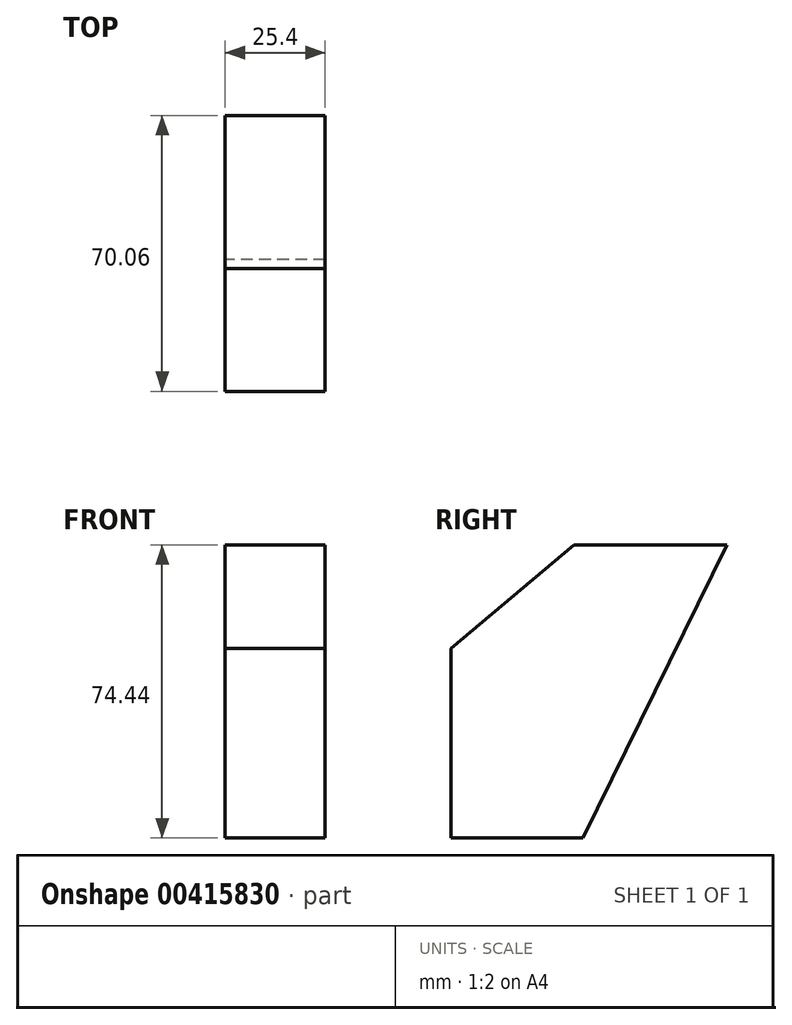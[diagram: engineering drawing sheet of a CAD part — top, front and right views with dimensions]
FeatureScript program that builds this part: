
annotation { "Feature Type Name" : "Feature", "Feature Type Description" : "" }
export const myFeature = defineFeature(function(context is Context, id is Id, definition is map)
    precondition{}
    {
        {
            var Q0;
            Q0=qCreatedBy(makeId("Right.planeOp"),FACE);
            var sketch = newSketch(context, id + "F0", { "sketchPlane" : qUnion([Q0])});
            skLineSegment(sketch, "E0.bottom", {"start": v(0, 0) * mm, "end": v(33.5, 0) * mm});
            skLineSegment(sketch, "E0.top", {"start": v(0, 48.1) * mm, "end": v(33.5, 48.1) * mm});
            skLineSegment(sketch, "E0.left", {"start": v(0, 0) * mm, "end": v(0, 48.1) * mm});
            skLineSegment(sketch, "E0.right", {"start": v(33.5, 0) * mm, "end": v(33.5, 48.1) * mm});
            skLineSegment(sketch, "E1", {"start": v(0, 48.1) * mm, "end": v(31.22, 74.44) * mm});
            skLineSegment(sketch, "E2", {"start": v(31.22, 74.44) * mm, "end": v(33.5, 48.1) * mm});
            skLineSegment(sketch, "E3", {"start": v(33.5, 48.1) * mm, "end": v(70.06, 74.44) * mm});
            skLineSegment(sketch, "E4", {"start": v(70.06, 74.44) * mm, "end": v(33.5, 0) * mm});
            skLineSegment(sketch, "E5", {"start": v(31.22, 74.44) * mm, "end": v(70.06, 74.44) * mm});
            skSolve(sketch);
        }
        {
            var Q0;
            Q0=makeQuery(id+"F0.imprint","IMPRINT",FACE,{"disambiguationData":[TD([[makeQuery(id+"F0.imprint","IMPRINT",EDGE,{"derivedFrom":sQuery(id+"F0.wireOp",EDGE,"E0.top")}),1.0]])]});
            var Q1;
            Q1=makeQuery(id+"F0.imprint","IMPRINT",FACE,{"disambiguationData":[TD([[makeQuery(id+"F0.imprint","IMPRINT",EDGE,{"derivedFrom":sQuery(id+"F0.wireOp",EDGE,"E2")}),1.0]])]});
            var Q2;
            Q2=makeQuery(id+"F0.imprint","IMPRINT",FACE,{"disambiguationData":[TD([[makeQuery(id+"F0.imprint","IMPRINT",EDGE,{"derivedFrom":sQuery(id+"F0.wireOp",EDGE,"E0.right")}),-1.0]])]});
            var Q3;
            Q3=makeQuery(id+"F0.imprint","IMPRINT",FACE,{"disambiguationData":[TD([[makeQuery(id+"F0.imprint","IMPRINT",EDGE,{"derivedFrom":sQuery(id+"F0.wireOp",EDGE,"E0.bottom")}),1.0]])]});
            extrude(context, id + "F1", {"entities" : qUnion([Q0, Q1, Q2, Q3]), "depth" : 25.4 * mm});
        }
    });
